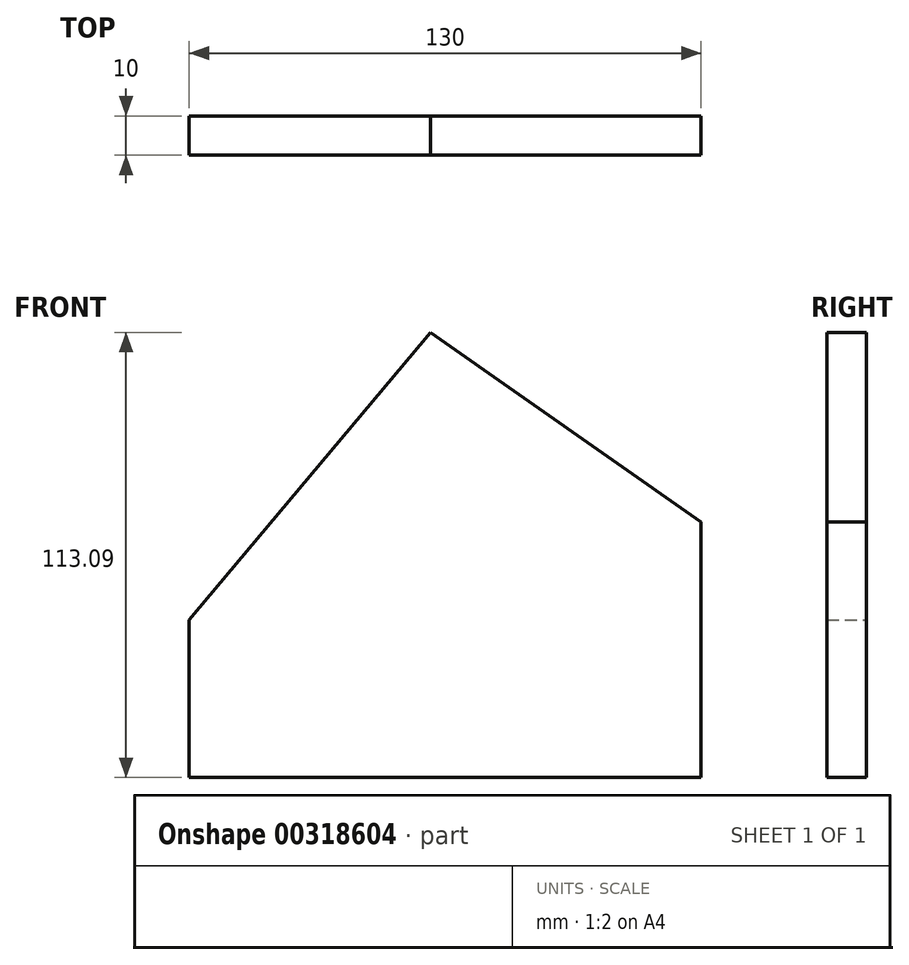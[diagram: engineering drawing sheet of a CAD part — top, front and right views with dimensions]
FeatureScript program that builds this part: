
annotation { "Feature Type Name" : "Feature", "Feature Type Description" : "" }
export const myFeature = defineFeature(function(context is Context, id is Id, definition is map)
    precondition{}
    {
        {
            var Q0;
            Q0=qCreatedBy(makeId("Front.planeOp"),FACE);
            var sketch = newSketch(context, id + "F0", { "sketchPlane" : qUnion([Q0])});
            skLineSegment(sketch, "E0", {"start": v(0, 0) * mm, "end": v(0, 65) * mm});
            skLineSegment(sketch, "E1", {"start": v(0, 65) * mm, "end": v(-68.67, 113.09) * mm});
            skLineSegment(sketch, "E2", {"start": v(-68.67, 113.09) * mm, "end": v(-130, 40) * mm});
            skLineSegment(sketch, "E3", {"start": v(-130, 40) * mm, "end": v(-130, 0) * mm});
            skLineSegment(sketch, "E4", {"start": v(-130, 0) * mm, "end": v(0, 0) * mm});
            skSolve(sketch);
        }
        {
            var Q0;
            Q0 = qSketchRegion(id + "F0", true);
            extrude(context, id + "F1", {"entities" : qUnion([Q0]), "depth" : 10 * mm});
        }
    });
